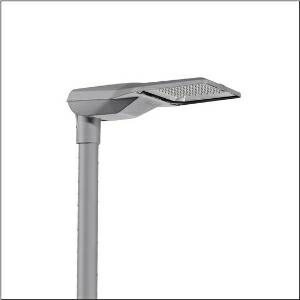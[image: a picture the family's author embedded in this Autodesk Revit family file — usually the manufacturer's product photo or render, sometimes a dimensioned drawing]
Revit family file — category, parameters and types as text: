
# Revit family: streetlight_sl_21_midi___st1_0ab_5xe7m33a08mb_9819
name_source: partatom
category: Lighting Fixtures
units: mm (PartAtom-declared; Revit-internal decimal feet)

## family parameters
Cut with Voids When Loaded = No
Host = Face
Light Source = No
Part Type = Normal
Room Calculation Point = No
Round Connector Dimension = Use Diameter
Shared = No

## types (1)
- --- (1 x LED, 16080 lm, 136 W, 3000K)
    Apparent Load = 136 VA
    CIE Flux Codes = 38 73 97 100 100
    Color Rendering = 70
    Color Temperature = 3000K
    Default Elevation = 1800 mm
    Description = Streetlight SL 21 midi, mast luminaire, primary light control with lens, of PMMA, primary optical cover: cover, of toughened safety glass, transparent, light distribution: ST1.0aB, light emission: direct distribution, primary light characteristic: asymmetric, installation type: post-top, side-entry, LED, 3G 1.5mm², High Power LED, rated luminous flux: 16.080lm, luminous efficacy: 118lm/W, light colour: 730, colour temperature: 3000K, control gear: Easy, control: flexible luminous flux parameterisation, time-dependent luminous flux control, constant luminous flux control, overheat protection, mains connection: 220..240V, AC, 50/60Hz, connection cable pre-assembled, cable length: 12,5m, wiring characteristics: H07RN-F, start of lifetime: 136W, end of service life: 142W, reduction: 61W, luminaire housing, of diecast aluminium, powder-coated, Siteco® metallic grey (DB 702S), corrosivity category C5 mid according to DIN EN ISO 12944, please order mast flange separately, inclination adjustable: 0°, 5°, 10°, 15°, sealing non-destructively replaceable, multi-level sealing system, length: 644mm, width: 335mm, height: 110mm, mast flange for spigot size: 42mm (side-entry): 5XC10008XM4, 60/48mm (side-entry/post-top): 5XC10108XM2, 76/60mm (side-entry/post-top): 5XC10108XM1, mounting height: 4..8m, protection rating (complete): IP66, insulation class (complete): insulation class II (safety insulation), certification: CE, ENEC, ENEC+, VDE, impact resistance: IK10, permissible operating ambient temperature for outdoor applications: -40..+50°C, standard-compliant lighting for roads and squares, packaging unit: 1 piece

Light Distribution: ST1.0aB
    Height = 111 mm
    Lamp = 1 x LED
    Lamp Light Flux = 16080 lm
    Lamp Power = 136 W
    Lamp count = 1
    Length = 644 mm
    Luminous efficacy = 118 lm/W
    Manufacturer = Siteco
    ModVariant = No
    Model = 5XE7M33A08MB
    Number of Poles = 1
    OnlyDefault = Yes
    Power Factor = 1
    Product Name = Streetlight SL 21 midi | ST1.0aB
    Product group = mast luminaire | pylon top
    ProductGroupID = 6100
    Protection Class = Protection class II
    Protection Degree = IP 66
    RLX_Detail_Level = 1
    RLX_Emergency_Light_Flux = 0 lm
    RLX_Emergency_Type = 0
    RLX_Emergency_Type_DB = No
    RlxData = <blob elided: 26733 chars, md5=f5cb8f52>
    Socket = socket
    Standby Power = 0 W
    System Light Flux = 16081 lm
    System Power = 136 W
    Type Comments = factory setting: luminous flux: 100 % | Output Level: 100 % | 695 mA
    Type Image = l_1004298.jpg
    URL = http://relux.com
    VarID = @adj_182804
    Voltage = 0 V
    Weight = 0.00 kg
    Width = 336 mm

## geometry (parser evidence)
native form markers: Blend x4, Sweep x9
no freeform markers — native parametric forms only
